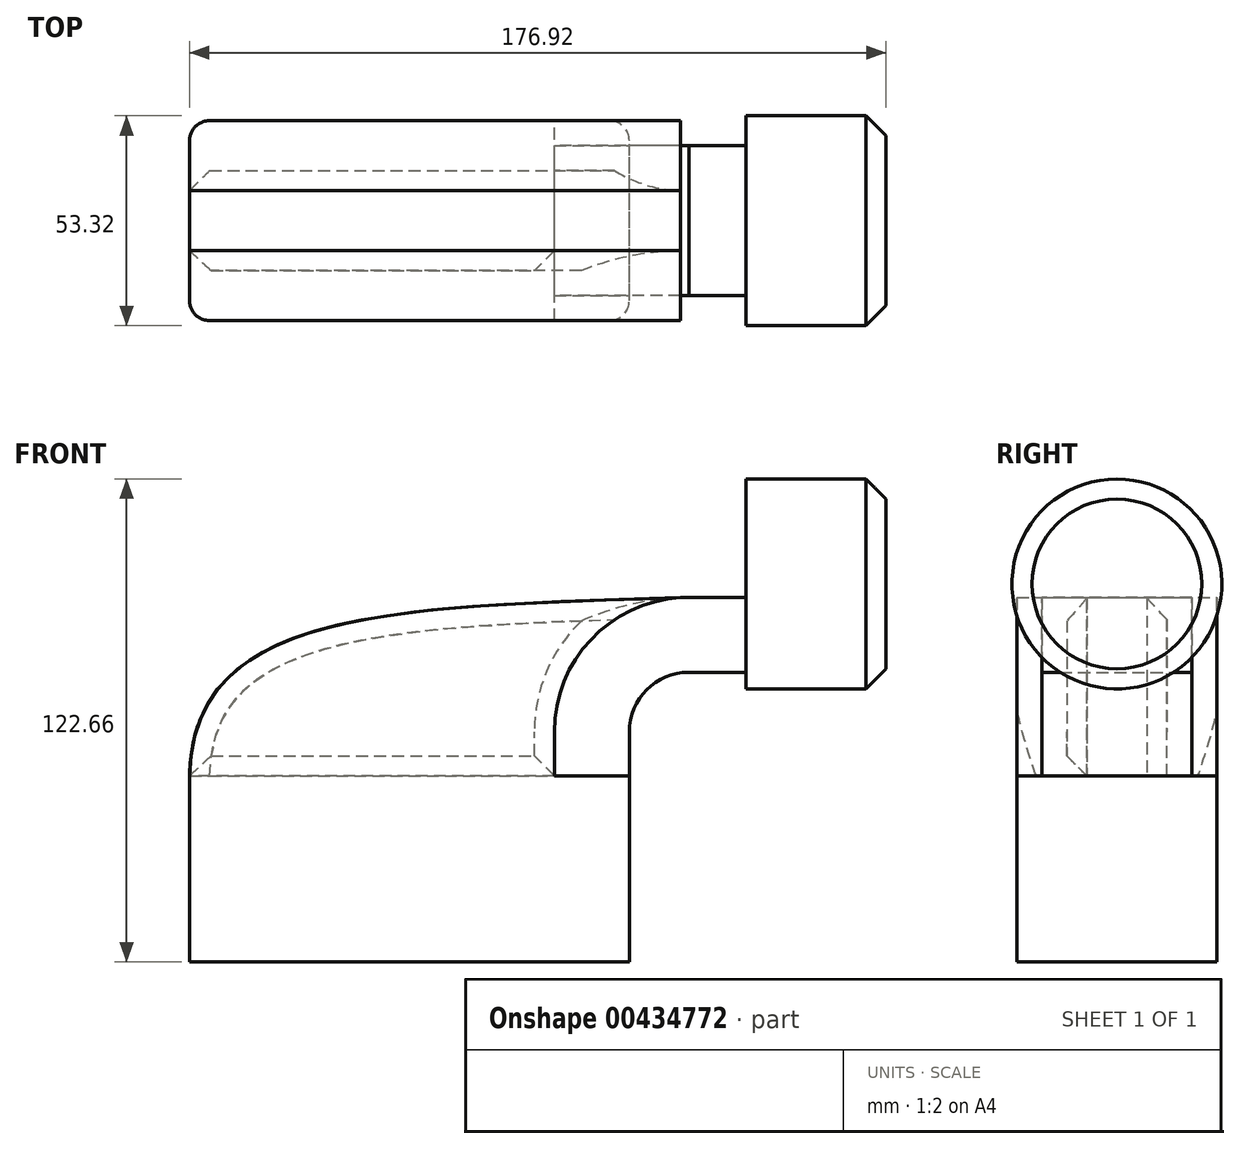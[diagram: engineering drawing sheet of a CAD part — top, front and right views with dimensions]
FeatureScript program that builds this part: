
annotation { "Feature Type Name" : "Feature", "Feature Type Description" : "" }
export const myFeature = defineFeature(function(context is Context, id is Id, definition is map)
    precondition{}
    {
        {
            var Q0;
            Q0=qCreatedBy(makeId("Front.planeOp"),FACE);
            var sketch = newSketch(context, id + "F0", { "sketchPlane" : qUnion([Q0])});
            skLineSegment(sketch, "E0.bottom", {"start": v(-55.85, -23.61) * mm, "end": v(55.85, -23.61) * mm});
            skLineSegment(sketch, "E0.top", {"start": v(-55.85, 23.61) * mm, "end": v(55.85, 23.61) * mm});
            skLineSegment(sketch, "E0.left", {"start": v(-55.85, -23.61) * mm, "end": v(-55.85, 23.61) * mm});
            skLineSegment(sketch, "E0.right", {"start": v(55.85, -23.61) * mm, "end": v(55.85, 23.61) * mm});
            skPoint(sketch, "E0.middle", {"position": v(0, 0) * mm});
            skLineSegment(sketch, "E1.bottom", {"start": v(121.07, 45.74) * mm, "end": v(85.53, 45.74) * mm});
            skLineSegment(sketch, "E1.top", {"start": v(121.07, 72.4) * mm, "end": v(85.53, 72.4) * mm});
            skLineSegment(sketch, "E1.left", {"start": v(121.07, 45.74) * mm, "end": v(121.07, 72.4) * mm});
            skLineSegment(sketch, "E1.right", {"start": v(85.53, 45.74) * mm, "end": v(85.53, 72.4) * mm});
            skPoint(sketch, "E1.middle", {"position": v(103.3, 59.06) * mm});
            skLineSegment(sketch, "E2", {"start": v(55.85, 23.61) * mm, "end": v(55.85, 34.82) * mm});
            skArc(sketch, "E3", {"start": v(55.85, 34.82) * mm, "mid": v(60.28, 45.51) * mm, "end": v(70.97, 49.94) * mm});
            skLineSegment(sketch, "E4", {"start": v(70.97, 49.94) * mm, "end": v(99.43, 49.94) * mm});
            skLineSegment(sketch, "E5.0", {"start": v(70.97, 68.99) * mm, "end": v(99.43, 68.99) * mm});
            skArc(sketch, "E5.1", {"start": v(36.8, 34.82) * mm, "mid": v(46.8, 58.98) * mm, "end": v(70.97, 68.99) * mm});
            skLineSegment(sketch, "E5.2", {"start": v(36.8, 23.61) * mm, "end": v(36.8, 34.82) * mm});
            skFitSpline(sketch, "E6", {"points": [v(-55.85, 23.61) * mm, v(70.97, 68.99) * mm], "startDerivative": vector(2.48, 127.6) * mm, "endDerivative": vector(227.56, 7.13) * mm});
            skSolve(sketch);
        }
        {
            var Q0;
            {var subQ0=sQuery(id+"F0.wireOp",EDGE,"E6");var subQ1=sQuery(id+"F0.wireOp",EDGE,"E5.1");var subQ3=makeQuery(id+"F0.imprint","INTERSECT",VERTEX,{"derivedFrom":[subQ1,subQ0]});Q0=makeQuery(id+"F0.imprint","IMPRINT",FACE,{"disambiguationData":[TD([[makeQuery(id+"F0.imprint","IMPRINT",EDGE,{"disambiguationData":[TD([[subQ3,-1.0]])],"derivedFrom":subQ1}),-1.0]])]});}
            var Q1;
            Q1=makeQuery(id+"F0.imprint","IMPRINT",FACE,{"disambiguationData":[TD([[makeQuery(id+"F0.imprint","IMPRINT",EDGE,{"derivedFrom":sQuery(id+"F0.wireOp",EDGE,"E0.bottom")}),1.0]])]});
            extrude(context, id + "F1", {"entities" : qUnion([Q0, Q1]), "endBound" : BoundingType.SYMMETRIC, "depth" : 50.8 * mm});
        }
        {
            var Q0;
            {var subQ0=sQuery(id+"F0.wireOp",EDGE,"E2");Q0=makeQuery(id+"F0.imprint","IMPRINT",FACE,{"disambiguationData":[TD([[makeQuery(id+"F0.imprint","IMPRINT",EDGE,{"derivedFrom":subQ0}),1.0]])]});}
            extrude(context, id + "F2", {"entities" : qUnion([Q0]), "endBound" : BoundingType.SYMMETRIC, "depth" : 38.1 * mm});
        }
        {
            var Q0;
            {var subQ3=sQuery(id+"F0.wireOp",EDGE,"E5.2");Q0=makeQuery(id+"F0.imprint","IMPRINT",FACE,{"disambiguationData":[TD([[makeQuery(id+"F0.imprint","IMPRINT",EDGE,{"derivedFrom":subQ3}),1.0]])]});}
            extrude(context, id + "F3", {"entities" : qUnion([Q0]), "endBound" : BoundingType.SYMMETRIC, "depth" : 25.4 * mm});
        }
        {
            var Q0;
            {var subQ1=sQuery(id+"F0.wireOp",EDGE,"E1.bottom");Q0=makeQuery(id+"F0.imprint","IMPRINT",FACE,{"disambiguationData":[TD([[makeQuery(id+"F0.imprint","IMPRINT",EDGE,{"derivedFrom":subQ1}),-1.0]])]});}
            var Q1;
            Q1=sQuery(id+"F0.wireOp",EDGE,"E1.top");
            revolve(context, id + "F4", {"operationType" : NewBodyOperationType.ADD, "entities" : qUnion([Q0]), "axis" : qUnion([Q1]), "revolveType" : RevolveType.FULL});
        }
        {
            var Q0;
            Q0=makeQuery(id+"F1.opExtrude","CAP_EDGE",EDGE,{"disambiguationData":[OSD([sQuery(id+"F0.wireOp",EDGE,"E0.right")])],"isStart":true});
            var Q1;
            Q1=makeQuery(id+"F1.opExtrude","CAP_EDGE",EDGE,{"disambiguationData":[OSD([sQuery(id+"F0.wireOp",EDGE,"E0.left")])],"isStart":true});
            var Q2;
            Q2=makeQuery(id+"F1.opExtrude","CAP_EDGE",EDGE,{"disambiguationData":[OSD([sQuery(id+"F0.wireOp",EDGE,"E0.right")])],"isStart":false});
            var Q3;
            Q3=makeQuery(id+"F1.opExtrude","CAP_EDGE",EDGE,{"disambiguationData":[OSD([sQuery(id+"F0.wireOp",EDGE,"E0.left")])],"isStart":false});
            fillet(context, id + "F5", {"entities" : qUnion([Q0, Q1, Q2, Q3]), "radius" : 5.08 * mm, "tangentPropagation" : true, "allowEdgeOverflow" : false});
        }
        {
            var Q0;
            Q0=makeQuery(id+"F4.opRevolve","SWEPT_EDGE",EDGE,{"disambiguationData":[OSD([sQuery(id+"F0.wireOp",EDGE,"E1.bottom"),sQuery(id+"F0.wireOp",EDGE,"E1.left")])]});
            chamfer(context, id + "F6", {"entities" : qUnion([Q0]), "width" : 5.08 * mm, "tangentPropagation" : true});
        }
        {
            var Q0;
            Q0=makeQuery(id+"F3.opExtrude","CAP_EDGE",EDGE,{"disambiguationData":[OSD([sQuery(id+"F0.wireOp",EDGE,"E6")])],"isStart":false});
            var Q1;
            Q1=makeQuery(id+"F3.opExtrude","CAP_EDGE",EDGE,{"disambiguationData":[OSD([sQuery(id+"F0.wireOp",EDGE,"E6")])],"isStart":true});
            var Q2;
            Q2=makeQuery(id+"F3.opExtrude","CAP_FACE",FACE,{"disambiguationData":[OSD([sQuery(id+"F0.wireOp",EDGE,"E0.top"),sQuery(id+"F0.wireOp",EDGE,"E5.1"),sQuery(id+"F0.wireOp",EDGE,"E5.2"),sQuery(id+"F0.wireOp",EDGE,"E6")])],"isStart":false});
            chamfer(context, id + "F7", {"entities" : qUnion([Q0, Q1, Q2]), "width" : 5.08 * mm, "tangentPropagation" : true});
        }
    });
